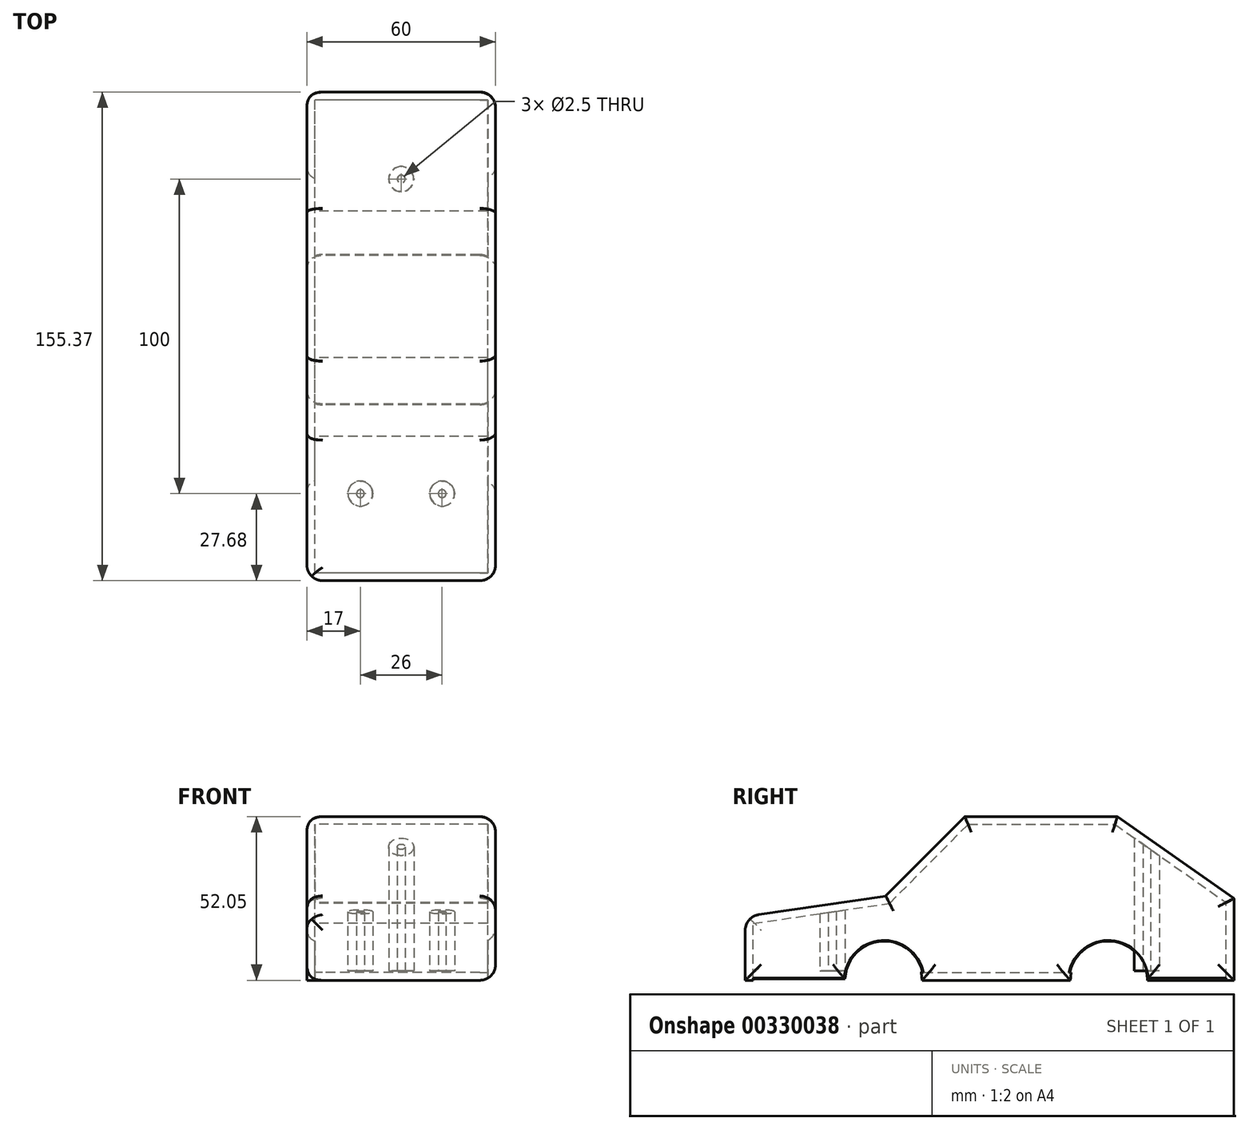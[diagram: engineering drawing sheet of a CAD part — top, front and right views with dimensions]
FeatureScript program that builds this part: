
annotation { "Feature Type Name" : "Feature", "Feature Type Description" : "" }
export const myFeature = defineFeature(function(context is Context, id is Id, definition is map)
    precondition{}
    {
        {
            var Q0;
            Q0=qCreatedBy(makeId("Right.planeOp"),FACE);
            var sketch = newSketch(context, id + "F0", { "sketchPlane" : qUnion([Q0])});
            skLineSegment(sketch, "E0.bottom", {"start": v(-69.8, 0) * mm, "end": v(85.56, 0) * mm});
            skLineSegment(sketch, "E0.top", {"start": v(-69.8, 52.05) * mm, "end": v(85.56, 52.05) * mm});
            skLineSegment(sketch, "E0.left", {"start": v(-69.8, 0) * mm, "end": v(-69.8, 52.05) * mm});
            skLineSegment(sketch, "E0.right", {"start": v(85.56, 0) * mm, "end": v(85.56, 52.05) * mm});
            skLineSegment(sketch, "E1", {"start": v(-69.8, 20.22) * mm, "end": v(-25.1, 26.8) * mm});
            skLineSegment(sketch, "E2", {"start": v(-25.1, 26.8) * mm, "end": v(0, 52.05) * mm});
            skLineSegment(sketch, "E3", {"start": v(48.53, 52.05) * mm, "end": v(85.56, 26.02) * mm});
            skCircle(sketch, "E4", {"center": v(-25.62, 0) * mm, "radius": 12 * mm});
            skCircle(sketch, "E5", {"center": v(45.6, 0) * mm, "radius": 12 * mm});
            skSolve(sketch);
        }
        {
            var Q0;
            Q0=qCreatedBy(makeId("Top.planeOp"),FACE);
            cPlane(context, id + "F1", {"entities" : qUnion([Q0]), "cplaneType" : CPlaneType.OFFSET, "offset" : 3 * mm, "width" : 152.4 * mm, "height" : 152.4 * mm});
        }
        {
            var Q0;
            Q0=qCreatedBy(id+"F1.planeOp",FACE);
            var sketch = newSketch(context, id + "F2", { "sketchPlane" : qUnion([Q0])});
            skCircle(sketch, "E6", {"center": v(0, 57.87) * mm, "radius": 4 * mm});
            skCircle(sketch, "E7", {"center": v(13, -42.13) * mm, "radius": 4 * mm});
            skCircle(sketch, "E8.MirrorC", {"center": v(-13, -42.13) * mm, "radius": 4 * mm});
            skLineSegment(sketch, "E9", {"start": v(0, 57.87) * mm, "end": v(0, -42.13) * mm, "construction": true});
            skLineSegment(sketch, "E10", {"start": v(13, -42.13) * mm, "end": v(0, -42.13) * mm, "construction": true});
            skPoint(sketch, "E11.orphan", {"position": v(0, -73.12) * mm});
            skCircle(sketch, "E12", {"center": v(0, 57.87) * mm, "radius": 1.25 * mm});
            skCircle(sketch, "E13", {"center": v(13, -42.13) * mm, "radius": 1.25 * mm});
            skCircle(sketch, "E14", {"center": v(-13, -42.13) * mm, "radius": 1.25 * mm});
            skSolve(sketch);
        }
        {
            var Q0;
            {var subQ1=sQuery(id+"F0.wireOp",EDGE,"E1");Q0=makeQuery(id+"F0.imprint","IMPRINT",FACE,{"disambiguationData":[TD([[makeQuery(id+"F0.imprint","IMPRINT",EDGE,{"derivedFrom":subQ1}),-1.0]])]});}
            extrude(context, id + "F3", {"entities" : qUnion([Q0]), "endBound" : BoundingType.SYMMETRIC, "depth" : 60 * mm});
        }
        {
            var Q0;
            {var subQ0=sQuery(id+"F0.wireOp",EDGE,"E0.bottom");var subQ1=makeQuery(id+"F0.imprint","IMPRINT",EDGE,{"disambiguationData":[TD([[makeQuery(id+"F0.imprint","INTERSECT",VERTEX,{"disambiguationData":[OD(1.0)],"derivedFrom":[subQ0,sQuery(id+"F0.wireOp",EDGE,"E4")]}),-1.0]])],"derivedFrom":subQ0});Q0=makeQuery(id+"FjavuCHx5vWW2yV_1.boolean.opBoolean","MERGE",FACE,{"derivedFrom":[makeQuery(id+"F3.opExtrude","SWEPT_FACE",FACE,{"disambiguationData":[OSD([subQ0]),TDD([subQ1])]}),makeQuery(id+"FjavuCHx5vWW2yV_1.opExtrude","SWEPT_FACE",FACE,{"disambiguationData":[OSD([subQ0]),TDD([makeQuery(id+"F3.opExtrude","CAP_EDGE",EDGE,{"disambiguationData":[OSD([subQ0]),TDD([subQ1])],"isStart":true})])]})]});}
            var Q1;
            {var subQ0=sQuery(id+"F0.wireOp",EDGE,"E0.bottom");var subQ1=makeQuery(id+"F0.imprint","IMPRINT",EDGE,{"disambiguationData":[TD([[makeQuery(id+"F0.imprint","INTERSECT",VERTEX,{"derivedFrom":[subQ0,sQuery(id+"F0.wireOp",EDGE,"E0.right")]}),1.0]])],"derivedFrom":subQ0});Q1=makeQuery(id+"FjavuCHx5vWW2yV_1.boolean.opBoolean","MERGE",FACE,{"derivedFrom":[makeQuery(id+"F3.opExtrude","SWEPT_FACE",FACE,{"disambiguationData":[OSD([subQ0]),TDD([subQ1])]}),makeQuery(id+"FjavuCHx5vWW2yV_1.opExtrude","SWEPT_FACE",FACE,{"disambiguationData":[OSD([subQ0]),TDD([makeQuery(id+"F3.opExtrude","CAP_EDGE",EDGE,{"disambiguationData":[OSD([subQ0]),TDD([subQ1])],"isStart":true})])]})]});}
            var Q2;
            {var subQ0=sQuery(id+"F0.wireOp",EDGE,"E5");Q2=makeQuery(id+"FjavuCHx5vWW2yV_1.boolean.opBoolean","MERGE",FACE,{"derivedFrom":[makeQuery(id+"F3.opExtrude","SWEPT_FACE",FACE,{"disambiguationData":[OSD([subQ0])]}),makeQuery(id+"FjavuCHx5vWW2yV_1.opExtrude","SWEPT_FACE",FACE,{"disambiguationData":[OSD([subQ0])]})]});}
            var Q3;
            {var subQ0=sQuery(id+"F0.wireOp",EDGE,"E4");Q3=makeQuery(id+"FjavuCHx5vWW2yV_1.boolean.opBoolean","MERGE",FACE,{"derivedFrom":[makeQuery(id+"F3.opExtrude","SWEPT_FACE",FACE,{"disambiguationData":[OSD([subQ0])]}),makeQuery(id+"FjavuCHx5vWW2yV_1.opExtrude","SWEPT_FACE",FACE,{"disambiguationData":[OSD([subQ0])]})]});}
            var Q4;
            {var subQ0=sQuery(id+"F0.wireOp",EDGE,"E0.bottom");var subQ1=makeQuery(id+"F0.imprint","IMPRINT",EDGE,{"disambiguationData":[TD([[makeQuery(id+"F0.imprint","INTERSECT",VERTEX,{"derivedFrom":[subQ0,sQuery(id+"F0.wireOp",EDGE,"E0.left")]}),-1.0]])],"derivedFrom":subQ0});Q4=makeQuery(id+"FjavuCHx5vWW2yV_1.boolean.opBoolean","MERGE",FACE,{"derivedFrom":[makeQuery(id+"F3.opExtrude","SWEPT_FACE",FACE,{"disambiguationData":[OSD([subQ0]),TDD([subQ1])]}),makeQuery(id+"FjavuCHx5vWW2yV_1.opExtrude","SWEPT_FACE",FACE,{"disambiguationData":[OSD([subQ0]),TDD([makeQuery(id+"F3.opExtrude","CAP_EDGE",EDGE,{"disambiguationData":[OSD([subQ0]),TDD([subQ1])],"isStart":true})])]})]});}
            shell(context, id + "F4", {"entities" : qUnion([Q0, Q1, Q2, Q3, Q4]), "thickness" : 2.5 * mm});
        }
        {
            var Q0;
            Q0 = qSketchRegion(id + "F2", true);
            var Q1;
            Q1=makeQuery(id+"F3.opExtrude","SWEPT_BODY",BODY,{"disambiguationData":[OSD([sQuery(id+"F0.wireOp",EDGE,"E0.bottom"),sQuery(id+"F0.wireOp",EDGE,"E0.top"),sQuery(id+"F0.wireOp",EDGE,"E0.left"),sQuery(id+"F0.wireOp",EDGE,"E0.right"),sQuery(id+"F0.wireOp",EDGE,"E1"),sQuery(id+"F0.wireOp",EDGE,"E2"),sQuery(id+"F0.wireOp",EDGE,"E3"),sQuery(id+"F0.wireOp",EDGE,"E4"),sQuery(id+"F0.wireOp",EDGE,"E5")])]});
            extrude(context, id + "F5", {"entities" : qUnion([Q0]), "operationType" : NewBodyOperationType.ADD, "endBound" : BoundingType.UP_TO_BODY, "endBoundEntityBody" : qUnion([Q1]), "depth" : 25 * mm});
        }
        {
            var Q0;
            Q0=makeQuery(id+"F3.opExtrude","CAP_EDGE",EDGE,{"disambiguationData":[OSD([sQuery(id+"F0.wireOp",EDGE,"E0.right")])],"isStart":false});
            var Q1;
            {var subQ0=sQuery(id+"F0.wireOp",EDGE,"E0.bottom");Q1=makeQuery(id+"F3.opExtrude","CAP_EDGE",EDGE,{"disambiguationData":[OSD([subQ0]),TDD([makeQuery(id+"F0.imprint","IMPRINT",EDGE,{"disambiguationData":[TD([[makeQuery(id+"F0.imprint","INTERSECT",VERTEX,{"derivedFrom":[subQ0,sQuery(id+"F0.wireOp",EDGE,"E0.right")]}),1.0]])],"derivedFrom":subQ0})])],"isStart":false});}
            var Q2;
            Q2=makeQuery(id+"F3.opExtrude","CAP_FACE",FACE,{"disambiguationData":[OSD([sQuery(id+"F0.wireOp",EDGE,"E0.bottom"),sQuery(id+"F0.wireOp",EDGE,"E0.top"),sQuery(id+"F0.wireOp",EDGE,"E0.left"),sQuery(id+"F0.wireOp",EDGE,"E0.right"),sQuery(id+"F0.wireOp",EDGE,"E1"),sQuery(id+"F0.wireOp",EDGE,"E2"),sQuery(id+"F0.wireOp",EDGE,"E3"),sQuery(id+"F0.wireOp",EDGE,"E4"),sQuery(id+"F0.wireOp",EDGE,"E5")])],"isStart":false});
            var Q3;
            Q3=makeQuery(id+"F3.opExtrude","SWEPT_EDGE",EDGE,{"disambiguationData":[OSD([sQuery(id+"F0.wireOp",EDGE,"E0.left"),sQuery(id+"F0.wireOp",EDGE,"E1")])]});
            var Q4;
            Q4=makeQuery(id+"F3.opExtrude","CAP_EDGE",EDGE,{"disambiguationData":[OSD([sQuery(id+"F0.wireOp",EDGE,"E0.left")])],"isStart":true});
            fillet(context, id + "F6", {"entities" : qUnion([Q0, Q1, Q2, Q3, Q4]), "radius" : 5 * mm, "tangentPropagation" : true, "allowEdgeOverflow" : false});
        }
        {
            var Q0;
            Q0=makeQuery(id+"F3.opExtrude","CAP_EDGE",EDGE,{"disambiguationData":[OSD([sQuery(id+"F0.wireOp",EDGE,"E3")])],"isStart":true});
            var Q1;
            Q1=makeQuery(id+"F3.opExtrude","CAP_EDGE",EDGE,{"disambiguationData":[OSD([sQuery(id+"F0.wireOp",EDGE,"E0.top")])],"isStart":true});
            var Q2;
            Q2=makeQuery(id+"F3.opExtrude","CAP_EDGE",EDGE,{"disambiguationData":[OSD([sQuery(id+"F0.wireOp",EDGE,"E2")])],"isStart":true});
            var Q3;
            Q3=makeQuery(id+"F3.opExtrude","CAP_EDGE",EDGE,{"disambiguationData":[OSD([sQuery(id+"F0.wireOp",EDGE,"E1")])],"isStart":true});
            var Q4;
            Q4=makeQuery(id+"F3.opExtrude","CAP_EDGE",EDGE,{"disambiguationData":[OSD([sQuery(id+"F0.wireOp",EDGE,"E4")])],"isStart":true});
            var Q5;
            {var subQ0=sQuery(id+"F0.wireOp",EDGE,"E0.bottom");Q5=makeQuery(id+"F3.opExtrude","CAP_EDGE",EDGE,{"disambiguationData":[OSD([subQ0]),TDD([makeQuery(id+"F0.imprint","IMPRINT",EDGE,{"disambiguationData":[TD([[makeQuery(id+"F0.imprint","INTERSECT",VERTEX,{"disambiguationData":[OD(1.0)],"derivedFrom":[subQ0,sQuery(id+"F0.wireOp",EDGE,"E4")]}),-1.0]])],"derivedFrom":subQ0})])],"isStart":true});}
            var Q6;
            Q6=makeQuery(id+"F3.opExtrude","CAP_EDGE",EDGE,{"disambiguationData":[OSD([sQuery(id+"F0.wireOp",EDGE,"E5")])],"isStart":true});
            var Q7;
            Q7=makeQuery(id+"F3.opExtrude","CAP_EDGE",EDGE,{"disambiguationData":[OSD([sQuery(id+"F0.wireOp",EDGE,"E0.right")])],"isStart":true});
            var Q8;
            {var subQ0=sQuery(id+"F0.wireOp",EDGE,"E0.bottom");Q8=makeQuery(id+"F3.opExtrude","CAP_EDGE",EDGE,{"disambiguationData":[OSD([subQ0]),TDD([makeQuery(id+"F0.imprint","IMPRINT",EDGE,{"disambiguationData":[TD([[makeQuery(id+"F0.imprint","INTERSECT",VERTEX,{"derivedFrom":[subQ0,sQuery(id+"F0.wireOp",EDGE,"E0.left")]}),-1.0]])],"derivedFrom":subQ0})])],"isStart":true});}
            fillet(context, id + "F7", {"entities" : qUnion([Q0, Q1, Q2, Q3, Q4, Q5, Q6, Q7, Q8]), "radius" : 5 * mm, "rho" : 0.5, "crossSection" : FilletCrossSection.CONIC, "allowEdgeOverflow" : false});
        }
        {
            var Q0;
            Q0=makeQuery(id+"F3.opExtrude","SWEPT_EDGE",EDGE,{"disambiguationData":[OSD([sQuery(id+"F0.wireOp",EDGE,"E1"),sQuery(id+"F0.wireOp",EDGE,"E2")])]});
            var Q1;
            Q1=makeQuery(id+"F3.opExtrude","SWEPT_EDGE",EDGE,{"disambiguationData":[OSD([sQuery(id+"F0.wireOp",EDGE,"E0.top"),sQuery(id+"F0.wireOp",EDGE,"E3")])]});
            var Q2;
            Q2=makeQuery(id+"F3.opExtrude","SWEPT_EDGE",EDGE,{"disambiguationData":[OSD([sQuery(id+"F0.wireOp",EDGE,"E0.top"),sQuery(id+"F0.wireOp",EDGE,"E2")])]});
            var Q3;
            Q3=makeQuery(id+"F3.opExtrude","SWEPT_EDGE",EDGE,{"disambiguationData":[OSD([sQuery(id+"F0.wireOp",EDGE,"E0.right"),sQuery(id+"F0.wireOp",EDGE,"E3")])]});
            fillet(context, id + "F8", {"entities" : qUnion([Q0, Q1, Q2, Q3]), "radius" : 0.12 * mm, "tangentPropagation" : true, "allowEdgeOverflow" : false});
        }
    });
